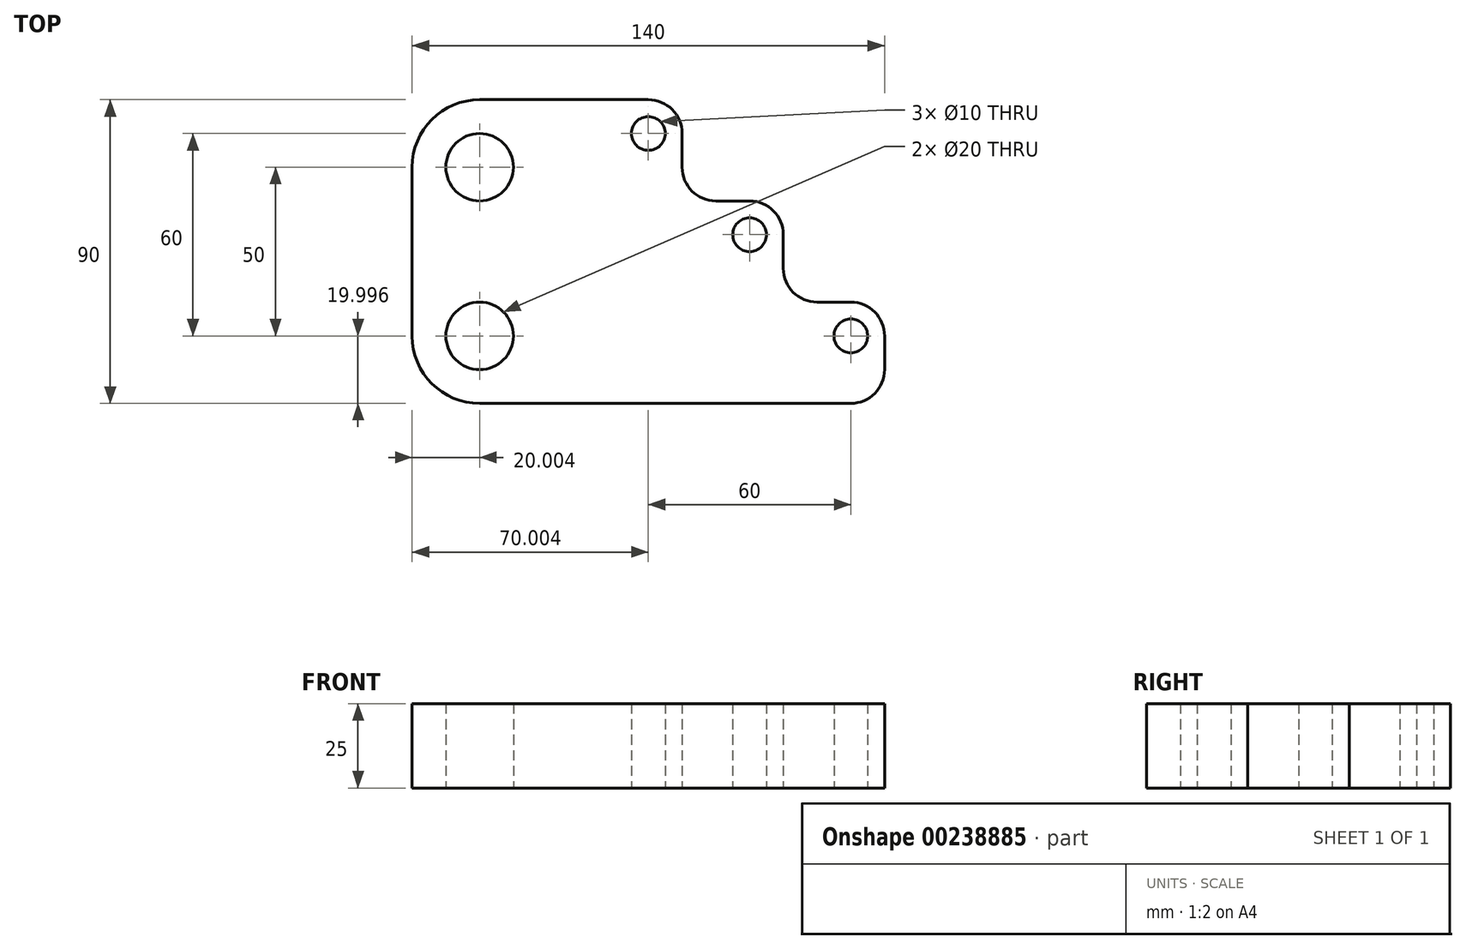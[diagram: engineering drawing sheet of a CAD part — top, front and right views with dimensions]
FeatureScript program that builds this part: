
annotation { "Feature Type Name" : "Feature", "Feature Type Description" : "" }
export const myFeature = defineFeature(function(context is Context, id is Id, definition is map)
    precondition{}
    {
        {
            var Q0;
            Q0=qCreatedBy(makeId("Top.planeOp"),FACE);
            var sketch = newSketch(context, id + "F0", { "sketchPlane" : qUnion([Q0])});
            skLineSegment(sketch, "E0", {"start": v(-31.87, -57.07) * mm, "end": v(78.13, -57.07) * mm});
            skLineSegment(sketch, "E1", {"start": v(88.13, -47.07) * mm, "end": v(88.13, -37.07) * mm});
            skLineSegment(sketch, "E2", {"start": v(78.13, -27.07) * mm, "end": v(68.13, -27.07) * mm});
            skLineSegment(sketch, "E3", {"start": v(58.13, -17.07) * mm, "end": v(58.13, -7.07) * mm});
            skLineSegment(sketch, "E4", {"start": v(48.13, 2.93) * mm, "end": v(38.13, 2.93) * mm});
            skLineSegment(sketch, "E5", {"start": v(28.13, 12.93) * mm, "end": v(28.13, 22.93) * mm});
            skLineSegment(sketch, "E6", {"start": v(18.13, 32.93) * mm, "end": v(-31.87, 32.93) * mm});
            skLineSegment(sketch, "E7", {"start": v(-51.87, 12.93) * mm, "end": v(-51.87, -37.07) * mm});
            skPoint(sketch, "E8.visualSharp", {"position": v(-51.87, -57.07) * mm});
            skArc(sketch, "E8.filletArc", {"start": v(-51.87, -37.07) * mm, "mid": v(-46, -51.22) * mm, "end": v(-31.87, -57.07) * mm});
            skPoint(sketch, "E9.visualSharp", {"position": v(-51.87, 32.93) * mm});
            skArc(sketch, "E9.filletArc", {"start": v(-31.87, 32.93) * mm, "mid": v(-46, 27.07) * mm, "end": v(-51.87, 12.93) * mm});
            skPoint(sketch, "E10.visualSharp", {"position": v(88.13, -57.07) * mm});
            skArc(sketch, "E10.filletArc", {"start": v(78.13, -57.07) * mm, "mid": v(85.2, -54.15) * mm, "end": v(88.13, -47.07) * mm});
            skPoint(sketch, "E11.visualSharp", {"position": v(88.13, -27.07) * mm});
            skArc(sketch, "E11.filletArc", {"start": v(88.13, -37.07) * mm, "mid": v(85.2, -30) * mm, "end": v(78.13, -27.07) * mm});
            skPoint(sketch, "E12.visualSharp", {"position": v(58.13, -27.07) * mm});
            skArc(sketch, "E12.filletArc", {"start": v(58.13, -17.07) * mm, "mid": v(61.06, -24.15) * mm, "end": v(68.13, -27.07) * mm});
            skPoint(sketch, "E13.visualSharp", {"position": v(58.13, 2.93) * mm});
            skArc(sketch, "E13.filletArc", {"start": v(58.13, -7.07) * mm, "mid": v(55.2, 0) * mm, "end": v(48.13, 2.93) * mm});
            skPoint(sketch, "E14.visualSharp", {"position": v(28.13, 2.93) * mm});
            skArc(sketch, "E14.filletArc", {"start": v(28.13, 12.93) * mm, "mid": v(31.06, 5.85) * mm, "end": v(38.13, 2.93) * mm});
            skPoint(sketch, "E15.visualSharp", {"position": v(28.13, 32.93) * mm});
            skArc(sketch, "E15.filletArc", {"start": v(28.13, 22.93) * mm, "mid": v(25.2, 30) * mm, "end": v(18.13, 32.93) * mm});
            skLineSegment(sketch, "E16", {"start": v(-51.87, -57.07) * mm, "end": v(-31.87, -57.07) * mm, "construction": true});
            skLineSegment(sketch, "E17", {"start": v(-31.87, -37.07) * mm, "end": v(-31.87, -57.07) * mm, "construction": true});
            skLineSegment(sketch, "E18", {"start": v(-51.87, -57.07) * mm, "end": v(-51.87, 12.93) * mm, "construction": true});
            skLineSegment(sketch, "E19", {"start": v(-31.87, 12.93) * mm, "end": v(-51.87, 12.93) * mm, "construction": true});
            skCircle(sketch, "E20", {"center": v(-31.87, 12.93) * mm, "radius": 10 * mm});
            skCircle(sketch, "E21", {"center": v(-31.87, -37.07) * mm, "radius": 10 * mm});
            skCircle(sketch, "E22", {"center": v(48.13, -7.07) * mm, "radius": 5 * mm});
            skCircle(sketch, "E23", {"center": v(78.13, -37.07) * mm, "radius": 5 * mm});
            skCircle(sketch, "E24", {"center": v(18.13, 22.93) * mm, "radius": 5 * mm});
            skSolve(sketch);
        }
        {
            var Q0;
            Q0 = qSketchRegion(id + "F0", true);
            extrude(context, id + "F1", {"entities" : qUnion([Q0]), "depth" : 25 * mm});
        }
    });
